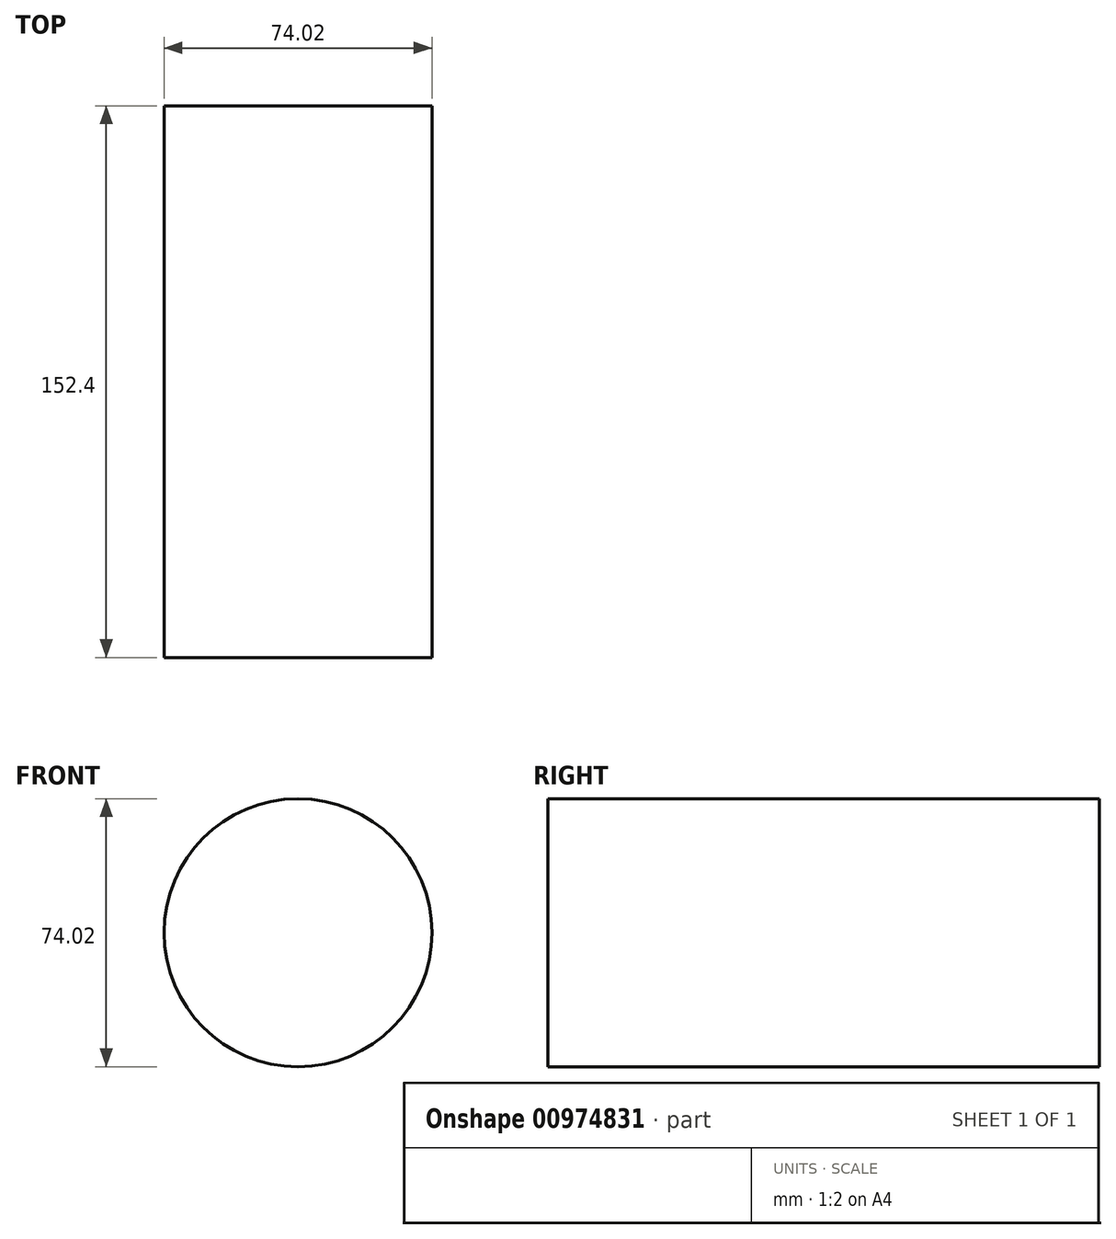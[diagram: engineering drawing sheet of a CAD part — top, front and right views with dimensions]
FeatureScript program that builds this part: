
annotation { "Feature Type Name" : "Feature", "Feature Type Description" : "" }
export const myFeature = defineFeature(function(context is Context, id is Id, definition is map)
    precondition{}
    {
        {
            var Q0;
            Q0=qCreatedBy(makeId("Front.planeOp"),FACE);
            var sketch = newSketch(context, id + "F0", { "sketchPlane" : qUnion([Q0])});
            skCircle(sketch, "E0", {"center": v(0, 0) * mm, "radius": 54.68 * mm});
            skSolve(sketch);
        }
        {
            var Q0;
            Q0=makeQuery(id+"F0.imprint","IMPRINT",FACE,{"disambiguationData":[TD([[makeQuery(id+"F0.imprint","IMPRINT",EDGE,{"derivedFrom":sQuery(id+"F0.wireOp",EDGE,"E0")}),1.0]])]});
            var sketch = newSketch(context, id + "F1", { "sketchPlane" : qUnion([Q0])});
            skCircle(sketch, "E1", {"center": v(0, 0) * mm, "radius": 37.01 * mm});
            skSolve(sketch);
        }
        {
            var Q0;
            Q0=makeQuery(id+"F1.imprint","IMPRINT",FACE,{"disambiguationData":[TD([[makeQuery(id+"F1.imprint","IMPRINT",EDGE,{"derivedFrom":sQuery(id+"F1.wireOp",EDGE,"E1")}),1.0]])]});
            extrude(context, id + "F2", {"entities" : qUnion([Q0]), "depth" : 152.4 * mm, "offsetDistance" : 30.48 * mm});
        }
        {
            var Q0;
            Q0=sQuery(id+"F0.wireOp",EDGE,"E0");
            extrude(context, id + "F3", {"bodyType" : ToolBodyType.SURFACE, "surfaceEntities" : qUnion([Q0]), "depth" : 50.8 * mm, "offsetDistance" : 30.48 * mm});
        }
    });
